# Revit family: 701330001_Griferia LavamanosPush Empotrar
name_source: partatom
category: Plumbing Fixtures
units: mm (PartAtom-declared; Revit-internal decimal feet)

## family parameters
Always vertical = Yes
Cut with Voids When Loaded = No
Host = Wall
OmniClass Number = 23.31.11.00
OmniClass Title = Faucets
Part Type = Normal
Room Calculation Point = No
Round Connector Dimension = Use Diameter
Shared = No

## types (1)
- Type 1
    Ciclo de Vida y Desempeño de la Descarga = 150,000 ciclos
    Creado por = BIMBAU
    Default Elevation = 0 mm  [stored 0 ft]
    Description = Un producto perfecto para las necesidades de las instituciones de alto tráfico al estar diseñada para un óptimo funcionamiento y durabilidad. Destaca por sus características antivandálicas y cierre automático temporizado.
    Diametro de Tuberia para la Instalacion = 1/2 pulgada NPT.
    Fecha de creación = 12/03/2021
    Flujo Maximo por Norma = 9,68 L/min - 0,49 L/Descarga.
    Flujo Real = 6,5 - 9,68 L/min - 0,33 - 0,49 L/Descarga.
    Garantía = 2 Años
    Manufacturer = Corona
    Material = Corona_Aluminio
    Material 2 = Corona_Cobre
    Model = Griferia de lavamanos push con pico de empotrar
    Peso Bruto aprox = 940gr. / 2,07Lb
    Peso Neto aprox = 840gr. / 1,85Lb.
    Presion Maxima Recomendada = 80 PSI
    Presion Minima Recomendada = 20 PSI
    Referencia = 101330001
    URL = https://corona.co

note: [stored X ft] marks values corroborated as IEEE doubles in the binary element streams (Revit-internal decimal feet)

## geometry (parser evidence)
native form markers: Sweep x10
no freeform markers — native parametric forms only
